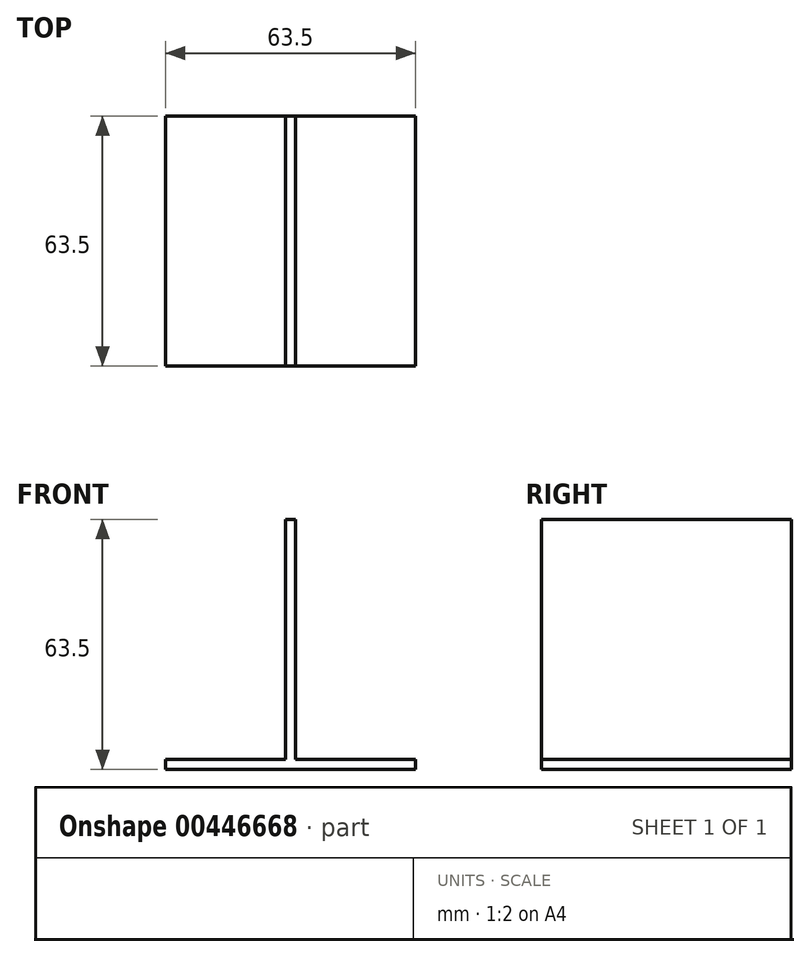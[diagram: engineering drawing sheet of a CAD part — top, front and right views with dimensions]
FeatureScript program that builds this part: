
annotation { "Feature Type Name" : "Feature", "Feature Type Description" : "" }
export const myFeature = defineFeature(function(context is Context, id is Id, definition is map)
    precondition{}
    {
        {
            var Q0;
            Q0=qCreatedBy(makeId("Front.planeOp"),FACE);
            var sketch = newSketch(context, id + "F0", { "sketchPlane" : qUnion([Q0])});
            skLineSegment(sketch, "E0", {"start": v(0, 0) * mm, "end": v(63.5, 0) * mm});
            skLineSegment(sketch, "E1", {"start": v(63.5, 0) * mm, "end": v(63.5, 2.54) * mm});
            skLineSegment(sketch, "E2", {"start": v(63.5, 2.54) * mm, "end": v(33.02, 2.54) * mm});
            skLineSegment(sketch, "E3", {"start": v(33.02, 2.54) * mm, "end": v(33.02, 63.5) * mm});
            skLineSegment(sketch, "E4", {"start": v(33.02, 63.5) * mm, "end": v(30.48, 63.5) * mm});
            skLineSegment(sketch, "E5", {"start": v(30.48, 63.5) * mm, "end": v(30.48, 2.54) * mm});
            skLineSegment(sketch, "E6", {"start": v(30.48, 2.54) * mm, "end": v(0, 2.54) * mm});
            skLineSegment(sketch, "E7", {"start": v(0, 2.54) * mm, "end": v(0, 0) * mm});
            skSolve(sketch);
        }
        {
            var Q0;
            Q0 = qSketchRegion(id + "F0", true);
            extrude(context, id + "F1", {"entities" : qUnion([Q0]), "depth" : 63.5 * mm, "offsetDistance" : 25.4 * mm});
        }
    });
